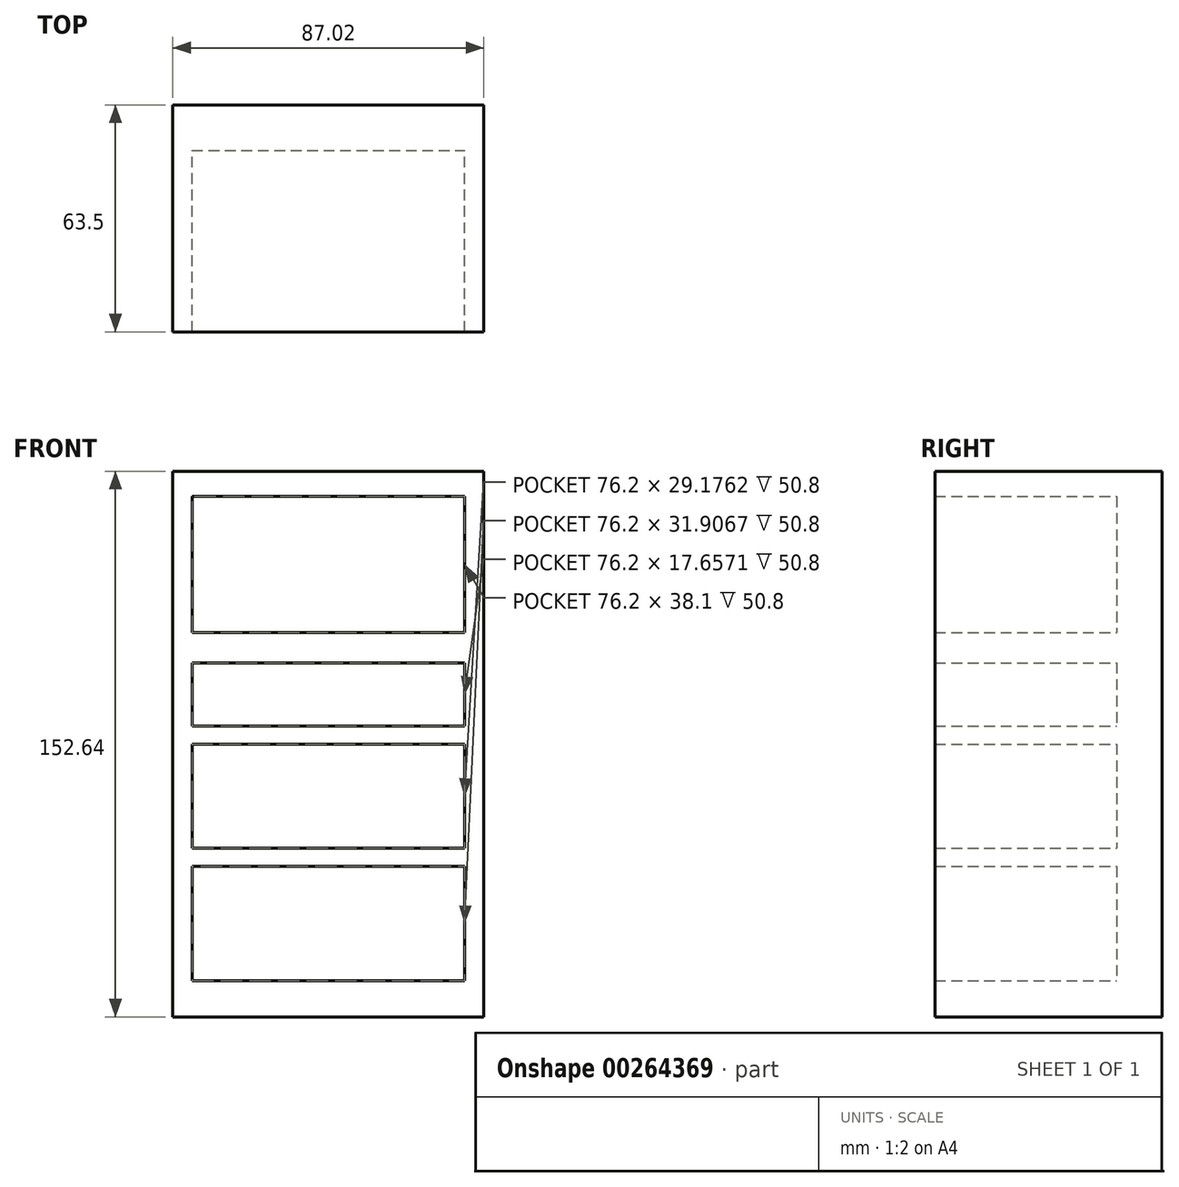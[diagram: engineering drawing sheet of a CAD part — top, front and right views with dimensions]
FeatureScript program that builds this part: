
annotation { "Feature Type Name" : "Feature", "Feature Type Description" : "" }
export const myFeature = defineFeature(function(context is Context, id is Id, definition is map)
    precondition{}
    {
        {
            var Q0;
            Q0=qCreatedBy(makeId("Front.planeOp"),FACE);
            var sketch = newSketch(context, id + "F0", { "sketchPlane" : qUnion([Q0])});
            skLineSegment(sketch, "E0.bottom", {"start": v(43.5, 76.32) * mm, "end": v(-43.5, 76.32) * mm});
            skLineSegment(sketch, "E0.top", {"start": v(43.5, -76.32) * mm, "end": v(-43.5, -76.32) * mm});
            skLineSegment(sketch, "E0.left", {"start": v(43.5, 76.32) * mm, "end": v(43.5, -76.32) * mm});
            skLineSegment(sketch, "E0.right", {"start": v(-43.5, 76.32) * mm, "end": v(-43.5, -76.32) * mm});
            skPoint(sketch, "E0.middle", {"position": v(0, 0) * mm});
            skSolve(sketch);
        }
        {
            var Q0;
            Q0=makeQuery(id+"F0.imprint","IMPRINT",FACE,{"disambiguationData":[TD([[makeQuery(id+"F0.imprint","IMPRINT",EDGE,{"derivedFrom":sQuery(id+"F0.wireOp",EDGE,"E0.bottom")}),1.0]])]});
            extrude(context, id + "F1", {"entities" : qUnion([Q0]), "depth" : 12.7 * mm});
        }
        {
            var Q0;
            Q0=makeQuery(id+"F1.opExtrude","CAP_FACE",FACE,{"disambiguationData":[OSD([sQuery(id+"F0.wireOp",EDGE,"E0.bottom"),sQuery(id+"F0.wireOp",EDGE,"E0.top"),sQuery(id+"F0.wireOp",EDGE,"E0.left"),sQuery(id+"F0.wireOp",EDGE,"E0.right")])],"isStart":false});
            var sketch = newSketch(context, id + "F2", { "sketchPlane" : qUnion([Q0])});
            skLineSegment(sketch, "E1.bottom", {"start": v(38.1, 69.24) * mm, "end": v(-38.1, 69.24) * mm});
            skLineSegment(sketch, "E1.top", {"start": v(38.1, 31.14) * mm, "end": v(-38.1, 31.14) * mm});
            skLineSegment(sketch, "E1.left", {"start": v(38.1, 69.24) * mm, "end": v(38.1, 31.14) * mm});
            skLineSegment(sketch, "E1.right", {"start": v(-38.1, 69.24) * mm, "end": v(-38.1, 31.14) * mm});
            skPoint(sketch, "E1.middle", {"position": v(0, 50.19) * mm});
            skLineSegment(sketch, "E2.bottom", {"start": v(38.1, 22.74) * mm, "end": v(-38.1, 22.74) * mm});
            skLineSegment(sketch, "E2.top", {"start": v(38.1, -66.16) * mm, "end": v(-38.1, -66.16) * mm});
            skLineSegment(sketch, "E2.left", {"start": v(38.1, 22.74) * mm, "end": v(38.1, -66.16) * mm});
            skLineSegment(sketch, "E2.right", {"start": v(-38.1, 22.74) * mm, "end": v(-38.1, -66.16) * mm});
            skPoint(sketch, "E2.middle", {"position": v(0, -21.71) * mm});
            skLineSegment(sketch, "E3", {"start": v(-38.1, 5.08) * mm, "end": v(38.1, 5.08) * mm});
            skLineSegment(sketch, "E4", {"start": v(38.1, 5.08) * mm, "end": v(38.1, 0) * mm});
            skLineSegment(sketch, "E5", {"start": v(38.1, 0) * mm, "end": v(-38.1, 0) * mm});
            skLineSegment(sketch, "E6", {"start": v(-38.1, 0) * mm, "end": v(-38.1, 5.08) * mm});
            skLineSegment(sketch, "E7", {"start": v(-38.1, -29.18) * mm, "end": v(38.1, -29.18) * mm});
            skLineSegment(sketch, "E8", {"start": v(38.1, -29.18) * mm, "end": v(38.1, -34.26) * mm});
            skLineSegment(sketch, "E9", {"start": v(38.1, -34.26) * mm, "end": v(-38.1, -34.26) * mm});
            skLineSegment(sketch, "E10", {"start": v(-38.1, -34.26) * mm, "end": v(-38.1, -29.18) * mm});
            skSolve(sketch);
        }
        {
            var Q0;
            Q0=makeQuery(id+"F2.imprint","IMPRINT",FACE,{"disambiguationData":[TD([[makeQuery(id+"F2.imprint","IMPRINT",EDGE,{"derivedFrom":sQuery(id+"F2.wireOp",EDGE,"E1.bottom")}),-1.0]])]});
            extrude(context, id + "F3", {"entities" : qUnion([Q0]), "operationType" : NewBodyOperationType.ADD, "depth" : 50.8 * mm});
        }
        {
            var Q0;
            Q0=makeQuery(id+"F2.imprint","IMPRINT",FACE,{"disambiguationData":[TD([[makeQuery(id+"F2.imprint","IMPRINT",EDGE,{"derivedFrom":sQuery(id+"F2.wireOp",EDGE,"E3")}),-1.0]])]});
            var Q1;
            Q1=makeQuery(id+"F2.imprint","IMPRINT",FACE,{"disambiguationData":[TD([[makeQuery(id+"F2.imprint","IMPRINT",EDGE,{"derivedFrom":sQuery(id+"F2.wireOp",EDGE,"E7")}),-1.0]])]});
            extrude(context, id + "F4", {"entities" : qUnion([Q0, Q1]), "operationType" : NewBodyOperationType.ADD, "depth" : 50.8 * mm});
        }
    });
